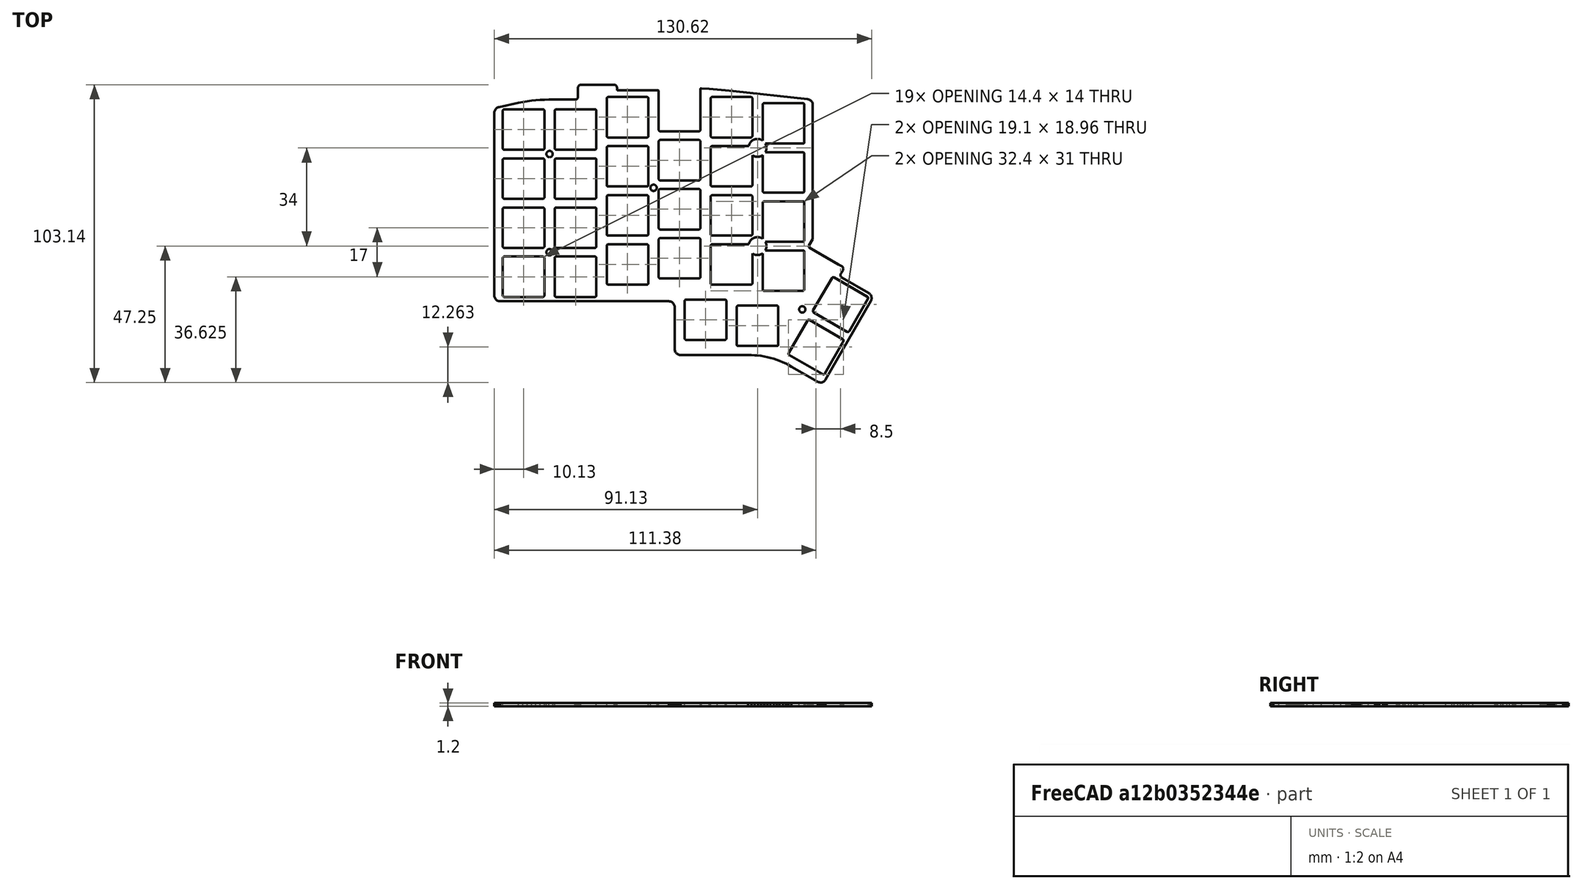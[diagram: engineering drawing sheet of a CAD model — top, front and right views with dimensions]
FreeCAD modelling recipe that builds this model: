
FCSTD DOCUMENT  (FreeCAD 0.19R)
Label: iris_case_mid_stl
License: All rights reserved
LicenseURL: http://en.wikipedia.org/wiki/All_rights_reserved
objects: Part::Feature×28, Part::Extrusion×28, App::LinkGroup×1, Part::FeaturePython×1
note: 57 computed .brp shape members not serialized (recipe doc carries the construction recipe); baked Part::Feature solids carry a one-line shape summary decoded from their .brp

FEATURE [Part::Feature] Face
  shape: bbox 130.6 x 103.1 x 2e-07 mm, 1 faces, 0 solids (baked)
FEATURE [Part::Feature] Face001 .. Face004  x4 (patterned run collapsed; names and placements below)
  shape: bbox 2.2 x 2.2 x 2e-07 mm, 1 faces, 0 solids (baked)
FEATURE [Part::Feature] Face005
  shape: bbox 19.11 x 18.96 x 2e-07 mm, 1 faces, 0 solids (baked)
FEATURE [Part::Feature] Face006 .. Face015  x10 (patterned run collapsed; names and placements below)
  shape: bbox 14.4 x 14 x 2e-07 mm, 1 faces, 0 solids (baked)
FEATURE [Part::Feature] Face016
  shape: bbox 32.4 x 31 x 2e-07 mm, 1 faces, 0 solids (baked)
FEATURE [Part::Feature] Face017
  shape: bbox 14.4 x 14 x 2e-07 mm, 1 faces, 0 solids (baked)
FEATURE [Part::Feature] Face018
  shape: bbox 19.11 x 18.96 x 2e-07 mm, 1 faces, 0 solids (baked)
FEATURE [Part::Feature] Face019
  shape: bbox 14.4 x 14 x 2e-07 mm, 1 faces, 0 solids (baked)
FEATURE [Part::Feature] Face020
  shape: bbox 14.4 x 14 x 2e-07 mm, 1 faces, 0 solids (baked)
FEATURE [Part::Feature] Face021
  shape: bbox 14.4 x 14 x 2e-07 mm, 1 faces, 0 solids (baked)
FEATURE [Part::Feature] Face022
  shape: bbox 32.4 x 31 x 2e-07 mm, 1 faces, 0 solids (baked)
FEATURE [Part::Feature] Face023 .. Face027  x5 (patterned run collapsed; names and placements below)
  shape: bbox 14.4 x 14 x 2e-07 mm, 1 faces, 0 solids (baked)
FEATURE [Part::Extrusion] Extrude
  Base = -> Face
  Dir = (0,0,1)
  DirMode = 0
  FaceMakerClass = Part::FaceMakerBullseye
  LengthFwd = 1.2
  LengthRev = 0
  Solid = true
  Symmetric = false
FEATURE [Part::Extrusion] Extrude001
  Base = -> Face001
  Dir = (0,0,1)
  DirMode = 0
  FaceMakerClass = Part::FaceMakerBullseye
  LengthFwd = 1.2
  LengthRev = 0
  Solid = true
  Symmetric = false
FEATURE [Part::Extrusion] Extrude002
  Base = -> Face002
  Dir = (0,0,1)
  DirMode = 0
  FaceMakerClass = Part::FaceMakerBullseye
  LengthFwd = 1.2
  LengthRev = 0
  Solid = true
  Symmetric = false
FEATURE [Part::Extrusion] Extrude003
  Base = -> Face003
  Dir = (0,0,1)
  DirMode = 0
  FaceMakerClass = Part::FaceMakerBullseye
  LengthFwd = 1.2
  LengthRev = 0
  Solid = true
  Symmetric = false
FEATURE [Part::Extrusion] Extrude004
  Base = -> Face004
  Dir = (0,0,1)
  DirMode = 0
  FaceMakerClass = Part::FaceMakerBullseye
  LengthFwd = 1.2
  LengthRev = 0
  Solid = true
  Symmetric = false
FEATURE [Part::Extrusion] Extrude005
  Base = -> Face005
  Dir = (0,0,1)
  DirMode = 0
  FaceMakerClass = Part::FaceMakerBullseye
  LengthFwd = 1.2
  LengthRev = 0
  Solid = true
  Symmetric = false
FEATURE [Part::Extrusion] Extrude006
  Base = -> Face006
  Dir = (0,0,1)
  DirMode = 0
  FaceMakerClass = Part::FaceMakerBullseye
  LengthFwd = 1.2
  LengthRev = 0
  Solid = true
  Symmetric = false
FEATURE [Part::Extrusion] Extrude007
  Base = -> Face007
  Dir = (0,0,1)
  DirMode = 0
  FaceMakerClass = Part::FaceMakerBullseye
  LengthFwd = 1.2
  LengthRev = 0
  Solid = true
  Symmetric = false
FEATURE [Part::Extrusion] Extrude008
  Base = -> Face008
  Dir = (0,0,1)
  DirMode = 0
  FaceMakerClass = Part::FaceMakerBullseye
  LengthFwd = 1.2
  LengthRev = 0
  Solid = true
  Symmetric = false
FEATURE [Part::Extrusion] Extrude009
  Base = -> Face009
  Dir = (0,0,1)
  DirMode = 0
  FaceMakerClass = Part::FaceMakerBullseye
  LengthFwd = 1.2
  LengthRev = 0
  Solid = true
  Symmetric = false
FEATURE [Part::Extrusion] Extrude010
  Base = -> Face010
  Dir = (0,0,1)
  DirMode = 0
  FaceMakerClass = Part::FaceMakerBullseye
  LengthFwd = 1.2
  LengthRev = 0
  Solid = true
  Symmetric = false
FEATURE [Part::Extrusion] Extrude011
  Base = -> Face011
  Dir = (0,0,1)
  DirMode = 0
  FaceMakerClass = Part::FaceMakerBullseye
  LengthFwd = 1.2
  LengthRev = 0
  Solid = true
  Symmetric = false
FEATURE [Part::Extrusion] Extrude012
  Base = -> Face012
  Dir = (0,0,1)
  DirMode = 0
  FaceMakerClass = Part::FaceMakerBullseye
  LengthFwd = 1.2
  LengthRev = 0
  Solid = true
  Symmetric = false
FEATURE [Part::Extrusion] Extrude013
  Base = -> Face013
  Dir = (0,0,1)
  DirMode = 0
  FaceMakerClass = Part::FaceMakerBullseye
  LengthFwd = 1.2
  LengthRev = 0
  Solid = true
  Symmetric = false
FEATURE [Part::Extrusion] Extrude014
  Base = -> Face014
  Dir = (0,0,1)
  DirMode = 0
  FaceMakerClass = Part::FaceMakerBullseye
  LengthFwd = 1.2
  LengthRev = 0
  Solid = true
  Symmetric = false
FEATURE [Part::Extrusion] Extrude015
  Base = -> Face015
  Dir = (0,0,1)
  DirMode = 0
  FaceMakerClass = Part::FaceMakerBullseye
  LengthFwd = 1.2
  LengthRev = 0
  Solid = true
  Symmetric = false
FEATURE [Part::Extrusion] Extrude016
  Base = -> Face016
  Dir = (0,0,1)
  DirMode = 0
  FaceMakerClass = Part::FaceMakerBullseye
  LengthFwd = 1.2
  LengthRev = 0
  Solid = true
  Symmetric = false
FEATURE [Part::Extrusion] Extrude017
  Base = -> Face017
  Dir = (0,0,1)
  DirMode = 0
  FaceMakerClass = Part::FaceMakerBullseye
  LengthFwd = 1.2
  LengthRev = 0
  Solid = true
  Symmetric = false
FEATURE [Part::Extrusion] Extrude018
  Base = -> Face018
  Dir = (0,0,1)
  DirMode = 0
  FaceMakerClass = Part::FaceMakerBullseye
  LengthFwd = 1.2
  LengthRev = 0
  Solid = true
  Symmetric = false
FEATURE [Part::Extrusion] Extrude019
  Base = -> Face019
  Dir = (0,0,1)
  DirMode = 0
  FaceMakerClass = Part::FaceMakerBullseye
  LengthFwd = 1.2
  LengthRev = 0
  Solid = true
  Symmetric = false
FEATURE [Part::Extrusion] Extrude020
  Base = -> Face020
  Dir = (0,0,1)
  DirMode = 0
  FaceMakerClass = Part::FaceMakerBullseye
  LengthFwd = 1.2
  LengthRev = 0
  Solid = true
  Symmetric = false
FEATURE [Part::Extrusion] Extrude021
  Base = -> Face021
  Dir = (0,0,1)
  DirMode = 0
  FaceMakerClass = Part::FaceMakerBullseye
  LengthFwd = 1.2
  LengthRev = 0
  Solid = true
  Symmetric = false
FEATURE [Part::Extrusion] Extrude022
  Base = -> Face022
  Dir = (0,0,1)
  DirMode = 0
  FaceMakerClass = Part::FaceMakerBullseye
  LengthFwd = 1.2
  LengthRev = 0
  Solid = true
  Symmetric = false
FEATURE [Part::Extrusion] Extrude023
  Base = -> Face023
  Dir = (0,0,1)
  DirMode = 0
  FaceMakerClass = Part::FaceMakerBullseye
  LengthFwd = 1.2
  LengthRev = 0
  Solid = true
  Symmetric = false
FEATURE [Part::Extrusion] Extrude024
  Base = -> Face024
  Dir = (0,0,1)
  DirMode = 0
  FaceMakerClass = Part::FaceMakerBullseye
  LengthFwd = 1.2
  LengthRev = 0
  Solid = true
  Symmetric = false
FEATURE [Part::Extrusion] Extrude025
  Base = -> Face025
  Dir = (0,0,1)
  DirMode = 0
  FaceMakerClass = Part::FaceMakerBullseye
  LengthFwd = 1.2
  LengthRev = 0
  Solid = true
  Symmetric = false
FEATURE [Part::Extrusion] Extrude026
  Base = -> Face026
  Dir = (0,0,1)
  DirMode = 0
  FaceMakerClass = Part::FaceMakerBullseye
  LengthFwd = 1.2
  LengthRev = 0
  Solid = true
  Symmetric = false
FEATURE [Part::Extrusion] Extrude027
  Base = -> Face027
  Dir = (0,0,1)
  DirMode = 0
  FaceMakerClass = Part::FaceMakerBullseye
  LengthFwd = 1.2
  LengthRev = 0
  Solid = true
  Symmetric = false
FEATURE [App::LinkGroup] LinkGroup  label="keys_holes"
  ElementList = -> [Extrude001,Extrude002,Extrude003,Extrude004,Extrude005,Extrude006,Extrude007,Extrude008,Extrude009,Extrude010,Extrude011,Extrude012,Extrude013,Extrude014,Extrude015,Extrude016,Extrude017,Extrude018,Extrude019,Extrude020,Extrude021,Extrude022,Extrude023,Extrude024,Extrude025,Extrude026,Extrude027]
  LinkMode = 0
FEATURE [Part::FeaturePython] Cutout  # WARN: FeaturePython — macro-defined, semantics opaque (R4)
  Base = -> Extrude
  Tolerance = 0
  Tool = -> LinkGroup
